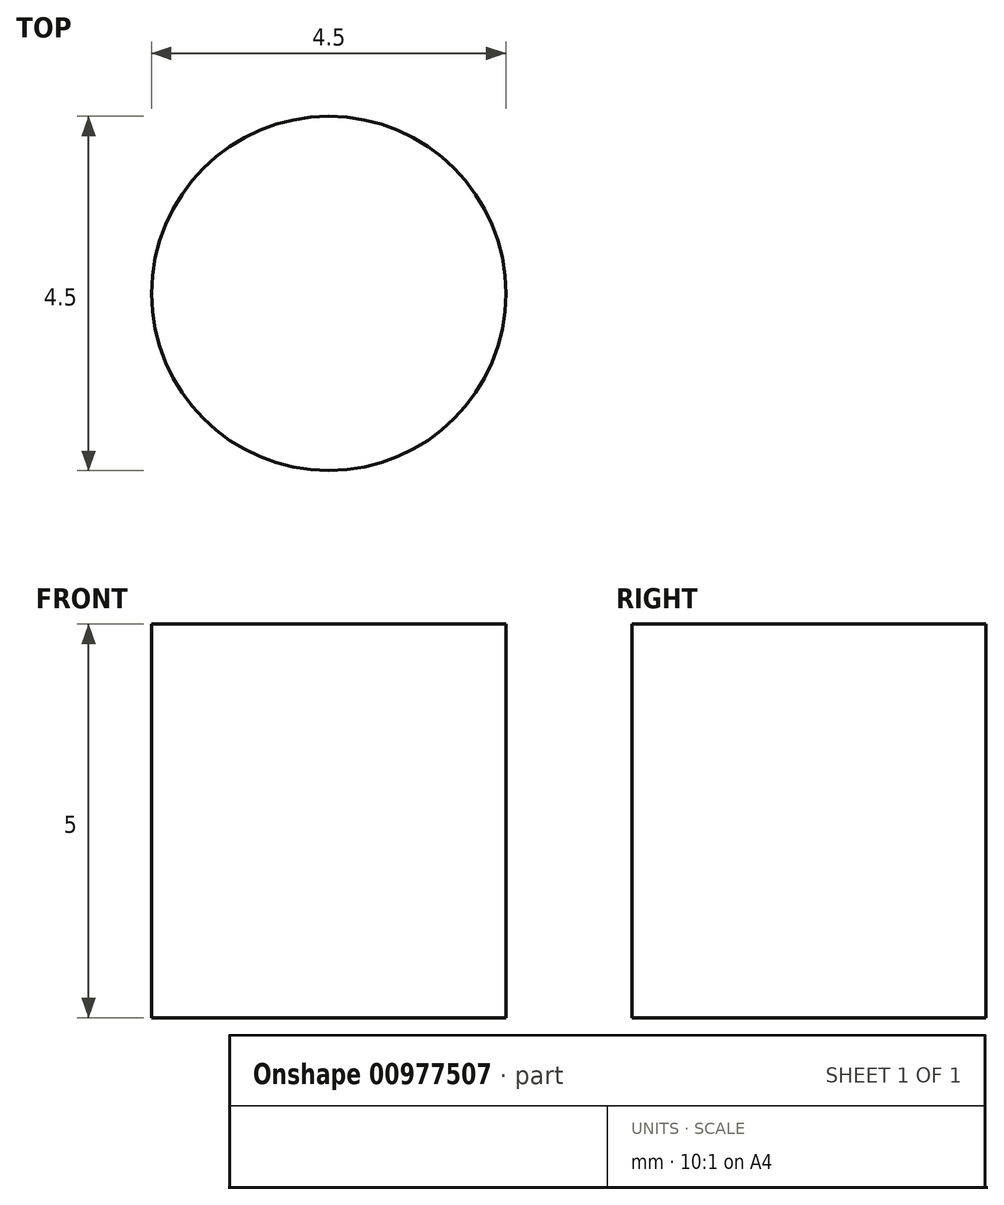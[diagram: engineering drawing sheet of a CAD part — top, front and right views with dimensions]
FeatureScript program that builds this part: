
annotation { "Feature Type Name" : "Feature", "Feature Type Description" : "" }
export const myFeature = defineFeature(function(context is Context, id is Id, definition is map)
    precondition{}
    {
        {
            var Q0;
            Q0=qCreatedBy(makeId("Top.planeOp"),FACE);
            var sketch = newSketch(context, id + "F0", { "sketchPlane" : qUnion([Q0])});
            skCircle(sketch, "E0", {"center": v(0, 0) * mm, "radius": 2.25 * mm});
            skSolve(sketch);
        }
        {
            var Q0;
            Q0 = qSketchRegion(id + "F0", true);
            extrude(context, id + "F1", {"entities" : qUnion([Q0]), "depth" : 5 * mm, "offsetDistance" : 25 * mm});
        }
    });
